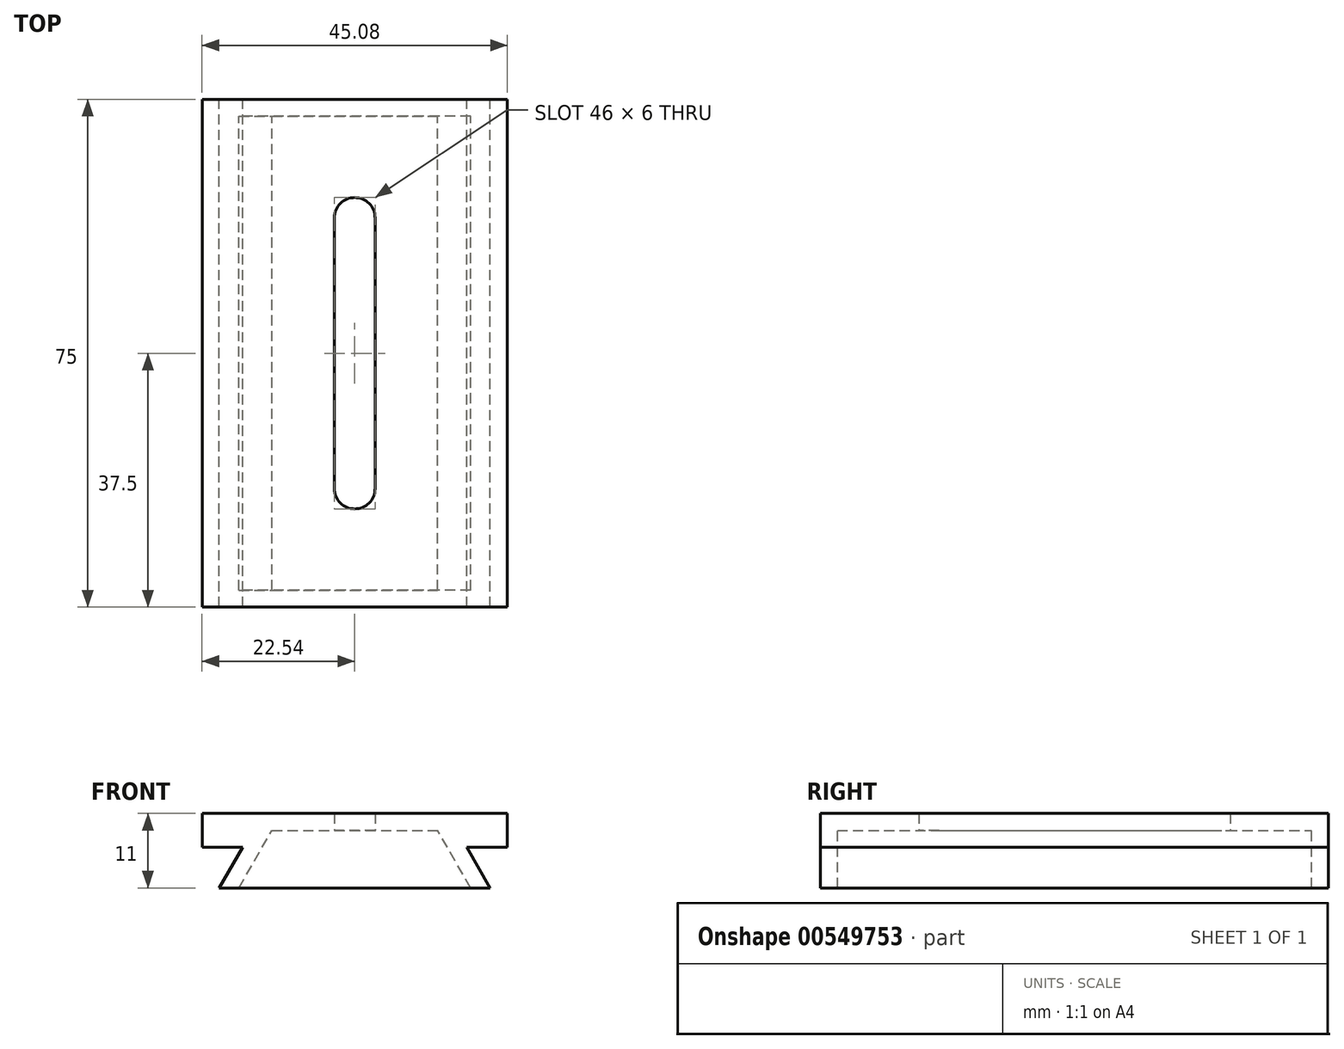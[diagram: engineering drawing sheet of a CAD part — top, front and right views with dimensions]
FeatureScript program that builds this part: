
annotation { "Feature Type Name" : "Feature", "Feature Type Description" : "" }
export const myFeature = defineFeature(function(context is Context, id is Id, definition is map)
    precondition{}
    {
        {
            var Q0;
            Q0=qCreatedBy(makeId("Front.planeOp"),FACE);
            var sketch = newSketch(context, id + "F0", { "sketchPlane" : qUnion([Q0])});
            skLineSegment(sketch, "E0.bottom", {"start": v(20, -3) * mm, "end": v(-20, -3) * mm});
            skPoint(sketch, "E0.middle", {"position": v(0, 0) * mm});
            skLineSegment(sketch, "E1", {"start": v(-20, -3) * mm, "end": v(-16.54, 3) * mm});
            skPoint(sketch, "E0.right.end.orphan", {"position": v(-20, 3) * mm});
            skLineSegment(sketch, "E2", {"start": v(20, -3) * mm, "end": v(16.54, 3) * mm});
            skPoint(sketch, "E0.left.end.orphan", {"position": v(20, 3) * mm});
            skLineSegment(sketch, "E3", {"start": v(-16.54, 3) * mm, "end": v(-22.54, 3) * mm});
            skLineSegment(sketch, "E4", {"start": v(-22.54, 3) * mm, "end": v(-22.54, 8) * mm});
            skLineSegment(sketch, "E5", {"start": v(-22.54, 8) * mm, "end": v(22.54, 8) * mm});
            skLineSegment(sketch, "E6", {"start": v(22.54, 8) * mm, "end": v(22.54, 3) * mm});
            skLineSegment(sketch, "E7", {"start": v(22.54, 3) * mm, "end": v(16.54, 3) * mm});
            skSolve(sketch);
        }
        {
            var Q0;
            Q0 = qSketchRegion(id + "F0", true);
            extrude(context, id + "F1", {"entities" : qUnion([Q0]), "endBound" : BoundingType.SYMMETRIC, "depth" : 75 * mm, "offsetDistance" : 25 * mm});
        }
        {
            var Q0;
            Q0=makeQuery(id+"F1.opExtrude","SWEPT_FACE",FACE,{"disambiguationData":[OSD([sQuery(id+"F0.wireOp",EDGE,"E0.bottom")])]});
            shell(context, id + "F2", {"entities" : qUnion([Q0]), "thickness" : 2.5 * mm});
        }
        {
            var Q0;
            Q0=makeQuery(id+"F2.opShell","OFFSET_FACE",FACE,{"disambiguationData":[OSD([sQuery(id+"F0.wireOp",EDGE,"E5")])]});
            var sketch = newSketch(context, id + "F3", { "sketchPlane" : qUnion([Q0])});
            skLineSegment(sketch, "E8.left", {"start": v(3, 20) * mm, "end": v(3, -20) * mm});
            skLineSegment(sketch, "E8.right", {"start": v(-3, 20) * mm, "end": v(-3, -20) * mm});
            skPoint(sketch, "E8.middle", {"position": v(0, 0) * mm});
            skArc(sketch, "E9", {"start": v(3, 20) * mm, "mid": v(0, 23) * mm, "end": v(-3, 20) * mm});
            skArc(sketch, "E10", {"start": v(-3, -20) * mm, "mid": v(0, -23) * mm, "end": v(3, -20) * mm});
            skSolve(sketch);
        }
        {
            var Q0;
            Q0 = qSketchRegion(id + "F3", true);
            extrude(context, id + "F4", {"entities" : qUnion([Q0]), "operationType" : NewBodyOperationType.REMOVE, "endBound" : BoundingType.UP_TO_NEXT, "oppositeDirection" : true, "depth" : 25 * mm, "offsetDistance" : 25 * mm});
        }
    });
